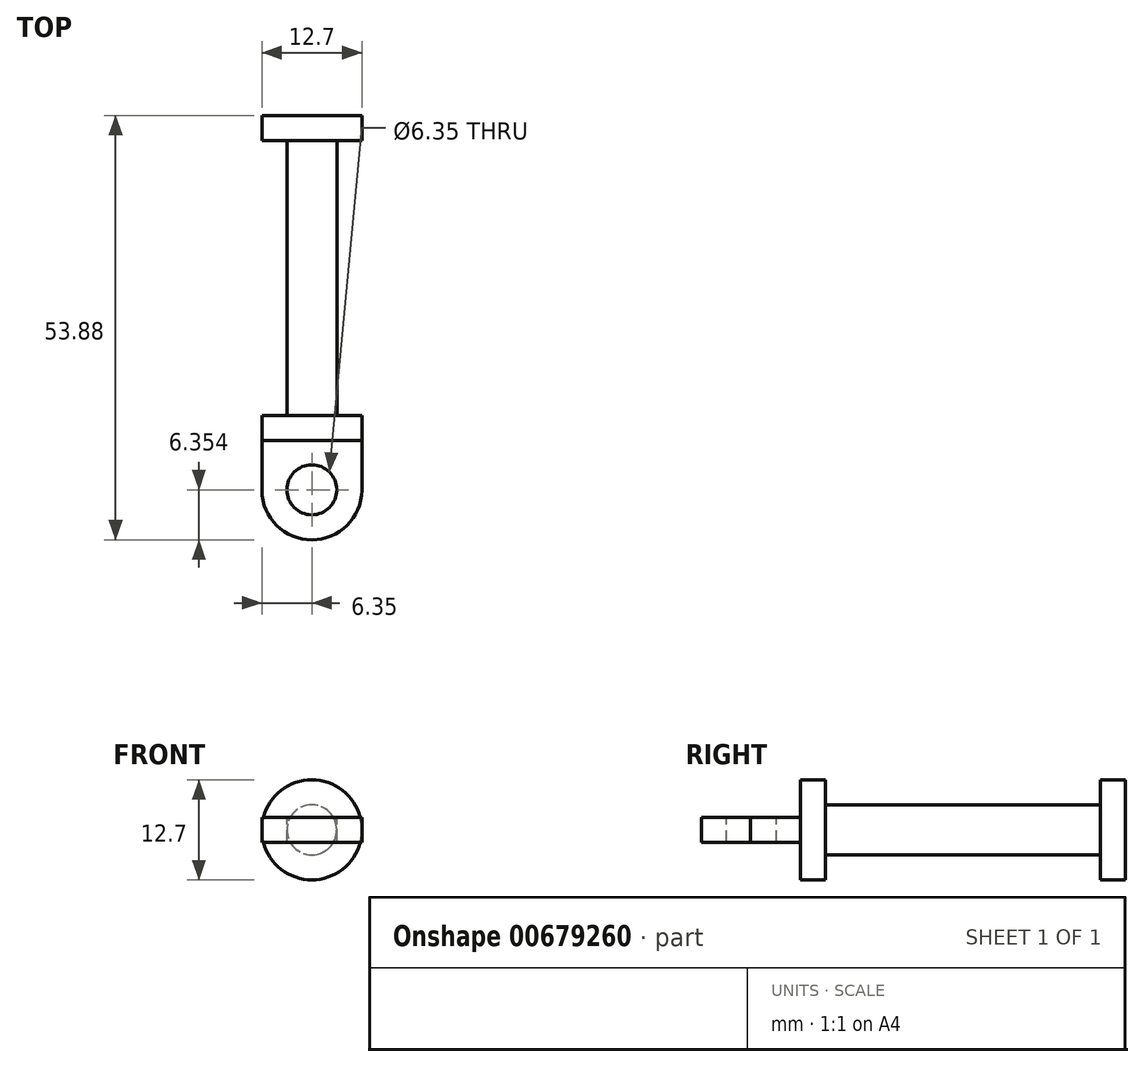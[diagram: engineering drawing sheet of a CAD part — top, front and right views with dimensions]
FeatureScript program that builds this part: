
annotation { "Feature Type Name" : "Feature", "Feature Type Description" : "" }
export const myFeature = defineFeature(function(context is Context, id is Id, definition is map)
    precondition{}
    {
        {
            var Q0;
            Q0=qCreatedBy(makeId("Front.planeOp"),FACE);
            var sketch = newSketch(context, id + "F0", { "sketchPlane" : qUnion([Q0])});
            skCircle(sketch, "E0", {"center": v(0, 0) * mm, "radius": 3.18 * mm});
            skSolve(sketch);
        }
        {
            var Q0;
            Q0=qSketchRegion(id+"F0",true);
            extrude(context, id + "F1", {"entities" : qUnion([Q0]), "depth" : 38.1 * mm, "offsetDistance" : 25.4 * mm});
        }
        {
            var Q0;
            Q0=makeQuery(id+"F1.opExtrude","CAP_FACE",FACE,{"disambiguationData":[OSD([sQuery(id+"F0.wireOp",EDGE,"E0")])],"isStart":true});
            var sketch = newSketch(context, id + "F2", { "sketchPlane" : qUnion([Q0])});
            skCircle(sketch, "E1", {"center": v(0, 0) * mm, "radius": 6.35 * mm});
            skSolve(sketch);
        }
        {
            var Q0;
            Q0=qSketchRegion(id+"F2",true);
            extrude(context, id + "F3", {"entities" : qUnion([Q0]), "operationType" : NewBodyOperationType.ADD, "depth" : 3.17 * mm, "offsetDistance" : 25.4 * mm});
        }
        {
            var Q0;
            Q0=makeQuery(id+"F1.opExtrude","CAP_FACE",FACE,{"disambiguationData":[OSD([sQuery(id+"F0.wireOp",EDGE,"E0")])],"isStart":false});
            var sketch = newSketch(context, id + "F4", { "sketchPlane" : qUnion([Q0])});
            skLineSegment(sketch, "E2.bottom", {"start": v(6.35, 1.59) * mm, "end": v(-6.35, 1.59) * mm});
            skLineSegment(sketch, "E2.top", {"start": v(6.35, -1.59) * mm, "end": v(-6.35, -1.59) * mm});
            skLineSegment(sketch, "E2.left", {"start": v(6.35, 1.59) * mm, "end": v(6.35, -1.59) * mm});
            skLineSegment(sketch, "E2.right", {"start": v(-6.35, 1.59) * mm, "end": v(-6.35, -1.59) * mm});
            skPoint(sketch, "E2.middle", {"position": v(0, 0) * mm});
            skSolve(sketch);
        }
        {
            var Q0;
            Q0=qSketchRegion(id+"F4",true);
            extrude(context, id + "F5", {"entities" : qUnion([Q0]), "operationType" : NewBodyOperationType.ADD, "depth" : 12.7 * mm, "offsetDistance" : 25.4 * mm});
        }
        {
            var Q0;
            Q0=makeQuery(id+"F5.opExtrude","SWEPT_FACE",FACE,{"disambiguationData":[OSD([sQuery(id+"F4.wireOp",EDGE,"E2.bottom")])]});
            var sketch = newSketch(context, id + "F6", { "sketchPlane" : qUnion([Q0])});
            skArc(sketch, "E3", {"start": v(-6.35, -44.45) * mm, "mid": v(0, -50.7) * mm, "end": v(6.35, -44.45) * mm});
            skLineSegment(sketch, "E4", {"start": v(-6.35, -44.45) * mm, "end": v(-6.35, -50.8) * mm});
            skLineSegment(sketch, "E5", {"start": v(-6.35, -50.8) * mm, "end": v(6.35, -50.8) * mm});
            skLineSegment(sketch, "E6", {"start": v(6.35, -50.8) * mm, "end": v(6.35, -44.45) * mm});
            skSolve(sketch);
        }
        {
            var Q0;
            Q0=qSketchRegion(id+"F6",true);
            extrude(context, id + "F7", {"entities" : qUnion([Q0]), "operationType" : NewBodyOperationType.REMOVE, "oppositeDirection" : true, "depth" : 25.4 * mm, "offsetDistance" : 25.4 * mm});
        }
        {
            var Q0;
            Q0=makeQuery(id+"F5.opExtrude","SWEPT_FACE",FACE,{"disambiguationData":[OSD([sQuery(id+"F4.wireOp",EDGE,"E2.bottom")])]});
            var sketch = newSketch(context, id + "F8", { "sketchPlane" : qUnion([Q0])});
            skCircle(sketch, "E7", {"center": v(0, -44.35) * mm, "radius": 3.18 * mm});
            skSolve(sketch);
        }
        {
            var Q0;
            Q0=qSketchRegion(id+"F8",true);
            extrude(context, id + "F9", {"entities" : qUnion([Q0]), "operationType" : NewBodyOperationType.REMOVE, "oppositeDirection" : true, "depth" : 25.4 * mm, "offsetDistance" : 25.4 * mm});
        }
        {
            var Q0;
            {var subQ0=sQuery(id+"F4.wireOp",EDGE,"E2.bottom");var subQ2=sQuery(id+"F4.wireOp",EDGE,"E2.top");var subQ3=sQuery(id+"F4.wireOp",EDGE,"E2.left");Q0=makeQuery(id+"F5.boolean.opBoolean","SPLIT",FACE,{"disambiguationData":[TD([makeQuery(id+"F5.opExtrude","SWEPT_FACE",FACE,{"disambiguationData":[OSD([subQ3])]})])],"derivedFrom":makeQuery(id+"F5.opExtrude","CAP_FACE",FACE,{"disambiguationData":[OSD([subQ0,subQ2,subQ3,sQuery(id+"F4.wireOp",EDGE,"E2.right")])],"isStart":true})});}
            var sketch = newSketch(context, id + "F10", { "sketchPlane" : qUnion([Q0])});
            skCircle(sketch, "E8", {"center": v(0, 0) * mm, "radius": 6.35 * mm});
            skSolve(sketch);
        }
        {
            var Q0;
            Q0=qSketchRegion(id+"F10",true);
            extrude(context, id + "F11", {"entities" : qUnion([Q0]), "operationType" : NewBodyOperationType.ADD, "depth" : 3.17 * mm, "offsetDistance" : 25.4 * mm});
        }
    });
